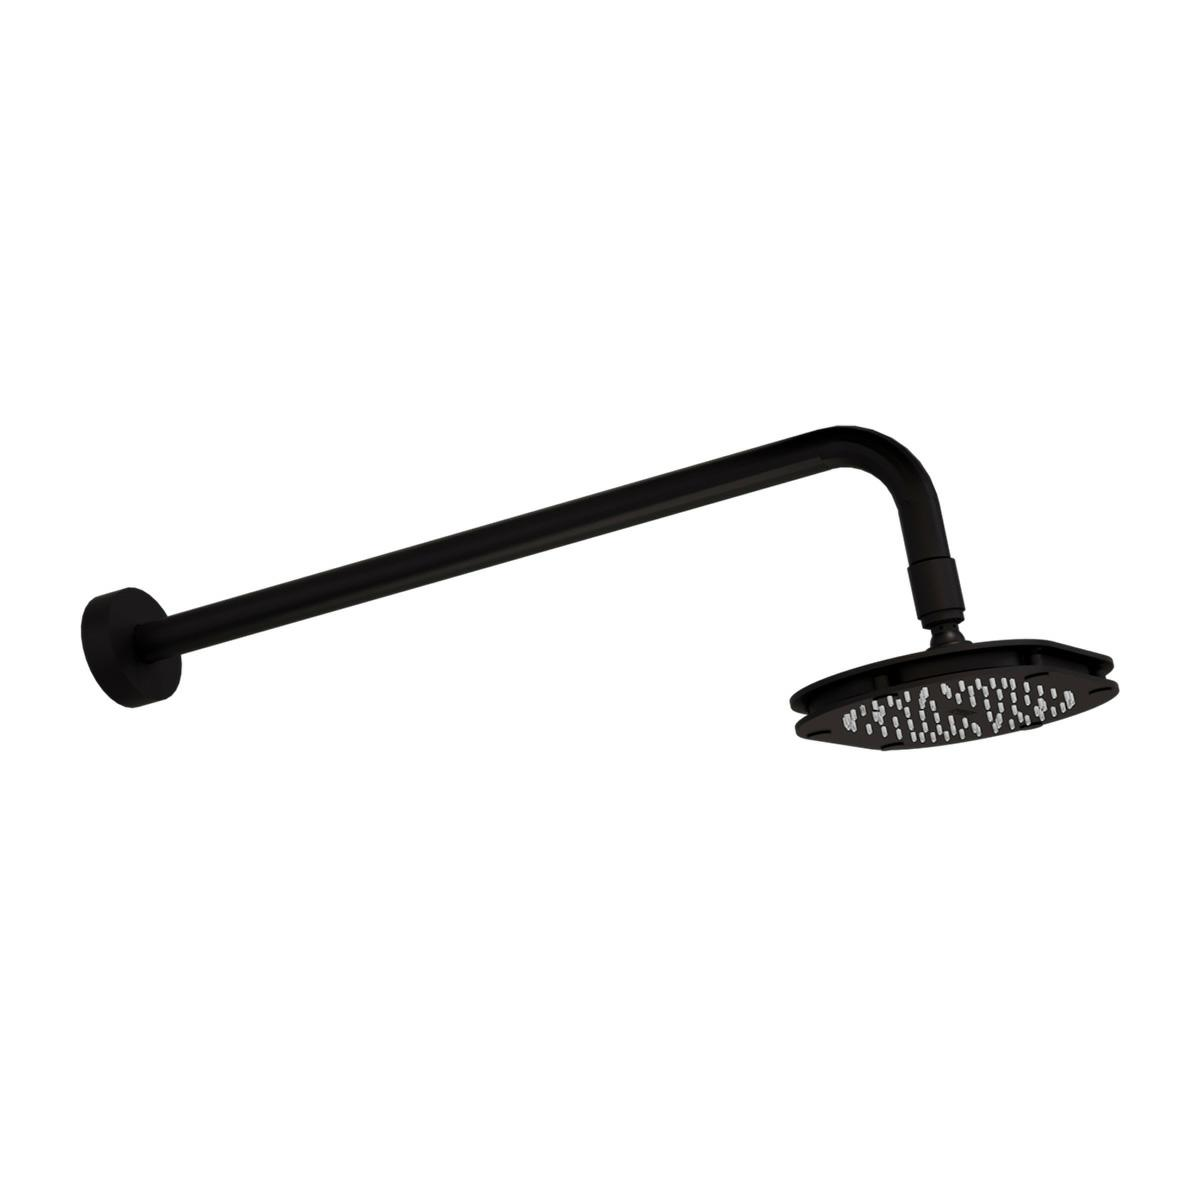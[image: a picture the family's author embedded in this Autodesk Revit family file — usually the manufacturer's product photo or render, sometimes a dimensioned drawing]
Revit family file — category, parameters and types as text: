
# Revit family: H3005-TR035-EB
name_source: partatom
category: Aparatos sanitarios
units: mm (PartAtom-declared; Revit-internal decimal feet)

## family parameters
Anfitrión = Cara
Compartido = Sí
Corte con vacíos al cargar = No
Cota de conector redondo = Diámetro de uso
Número OmniClass = 23.45.05.14.17
Punto de cálculo de habitación = Sí
Tipo de pieza = Normal
Título OmniClass = Showers

## types (2) — shared parameters
Conexión = ½"-14 NPSM
Elevación por defecto = 0.5 "
Fabricante = HELVEX S.A. DE C.V.
Imagen de tipo = H3005-TR035-EB.jpg
Presión máxima de trabajo = 85.3 psi
Presión mínima de trabajo = 14.2 psi
Total Diameter = 9.6 "
Total Length = 22.2 "

## per-type parameters (varying)
| type | Comentarios de tipo | Descripción | Material | Material EC | Modelo | URL |
| H3005-TR035 | Regadera redonda de plato ancho, multichorro 10"
3 Chorros.
3 Chorros. | Regadera redonda de plato ancho, multichorro 10"
3 Chorros.
3 Chorros. | 192_192_192 | <Por categoría> | H3005-TR035-EB |  |
| H3005-TR035-EB | Regadera de media y alta presión
3 Chorros.
3 Chorros. | Regadera de media y alta presión
3 Chorros.
3 Chorros. | Ébano | Ébano - Cromo | H3005-TR035 | https://www.helvex.com.mx |

## geometry (parser evidence)
native form markers: Sweep x6
no freeform markers — native parametric forms only
